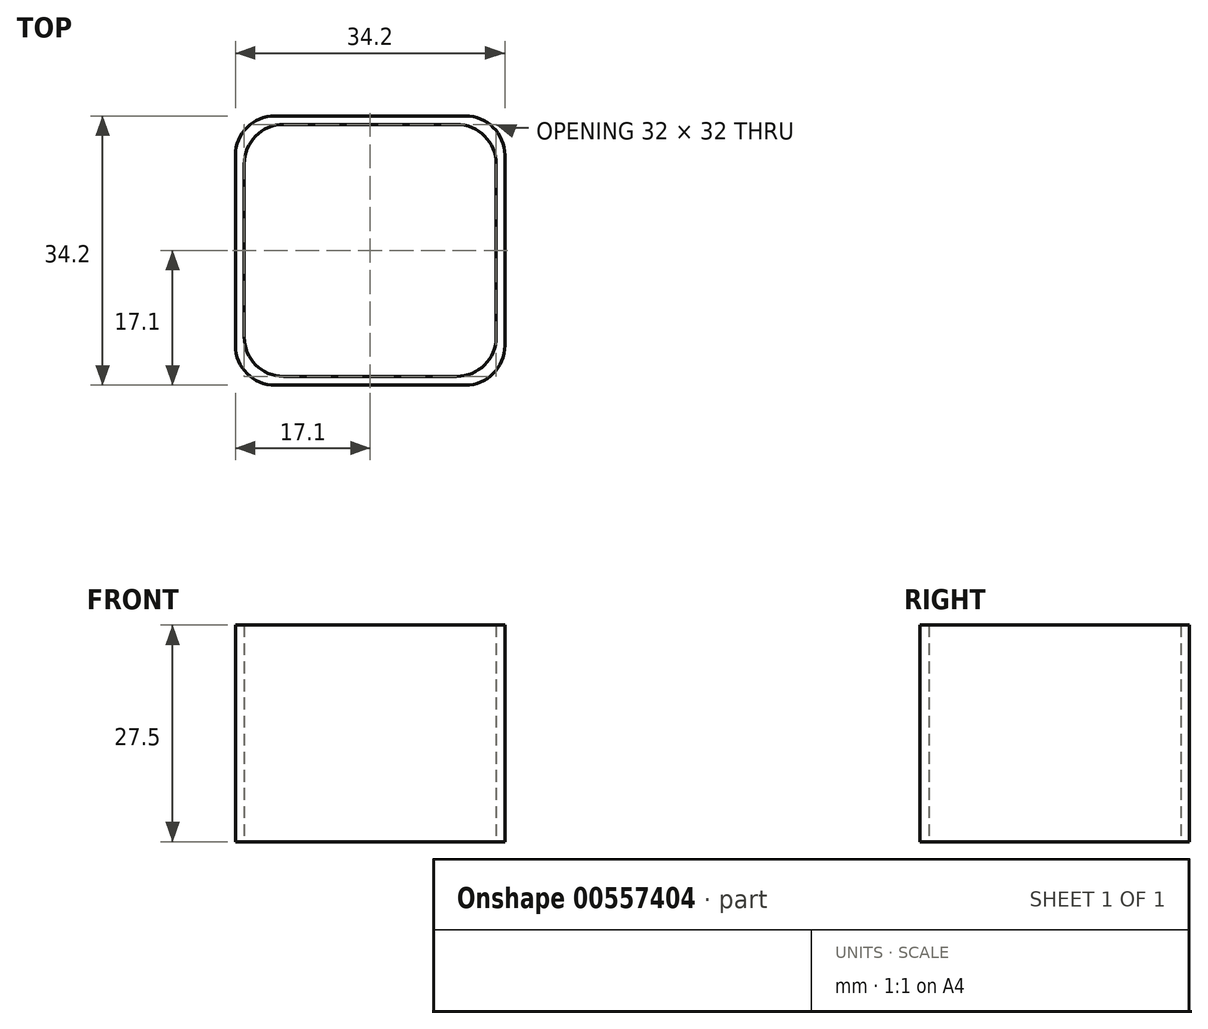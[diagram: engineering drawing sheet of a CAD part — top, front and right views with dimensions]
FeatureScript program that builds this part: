
annotation { "Feature Type Name" : "Feature", "Feature Type Description" : "" }
export const myFeature = defineFeature(function(context is Context, id is Id, definition is map)
    precondition{}
    {
        {
            var Q0;
            Q0=qCreatedBy(makeId("Top.planeOp"),FACE);
            var sketch = newSketch(context, id + "F0", { "sketchPlane" : qUnion([Q0])});
            skLineSegment(sketch, "E0.bottom", {"start": v(-17, 17) * mm, "end": v(15, 17) * mm});
            skLineSegment(sketch, "E0.top", {"start": v(-17, -15) * mm, "end": v(15, -15) * mm});
            skLineSegment(sketch, "E0.left", {"start": v(-17, 17) * mm, "end": v(-17, -15) * mm});
            skLineSegment(sketch, "E0.right", {"start": v(15, 17) * mm, "end": v(15, -15) * mm});
            skLineSegment(sketch, "E1.0", {"start": v(-15, 15) * mm, "end": v(13, 15) * mm, "construction": true});
            skLineSegment(sketch, "E1.1", {"start": v(-15, 15) * mm, "end": v(-15, -13) * mm, "construction": true});
            skLineSegment(sketch, "E1.2", {"start": v(-15, -13) * mm, "end": v(13, -13) * mm, "construction": true});
            skLineSegment(sketch, "E1.3", {"start": v(13, 15) * mm, "end": v(13, -13) * mm, "construction": true});
            skLineSegment(sketch, "E2.0", {"start": v(16.1, 18.1) * mm, "end": v(16.1, -16.1) * mm});
            skLineSegment(sketch, "E2.1", {"start": v(-18.1, 18.1) * mm, "end": v(16.1, 18.1) * mm});
            skLineSegment(sketch, "E2.2", {"start": v(-18.1, 18.1) * mm, "end": v(-18.1, -16.1) * mm});
            skLineSegment(sketch, "E2.3", {"start": v(-18.1, -16.1) * mm, "end": v(16.1, -16.1) * mm});
            skSolve(sketch);
        }
        {
            var Q0;
            Q0=makeQuery(id+"F0.imprint","IMPRINT",FACE,{"disambiguationData":[TD([[makeQuery(id+"F0.imprint","IMPRINT",EDGE,{"derivedFrom":sQuery(id+"F0.wireOp",EDGE,"E0.bottom")}),1.0]])]});
            extrude(context, id + "F1", {"entities" : qUnion([Q0]), "depth" : 27.5 * mm, "offsetDistance" : 25 * mm});
        }
        {
            var Q0;
            Q0=makeQuery(id+"F1.opExtrude","SWEPT_EDGE",EDGE,{"disambiguationData":[OSD([sQuery(id+"F0.wireOp",EDGE,"E2.0"),sQuery(id+"F0.wireOp",EDGE,"E2.3")])]});
            var Q1;
            Q1=makeQuery(id+"F1.opExtrude","SWEPT_EDGE",EDGE,{"disambiguationData":[OSD([sQuery(id+"F0.wireOp",EDGE,"E2.0"),sQuery(id+"F0.wireOp",EDGE,"E2.1")])]});
            var Q2;
            Q2=makeQuery(id+"F1.opExtrude","SWEPT_EDGE",EDGE,{"disambiguationData":[OSD([sQuery(id+"F0.wireOp",EDGE,"E2.2"),sQuery(id+"F0.wireOp",EDGE,"E2.3")])]});
            var Q3;
            Q3=makeQuery(id+"F1.opExtrude","SWEPT_EDGE",EDGE,{"disambiguationData":[OSD([sQuery(id+"F0.wireOp",EDGE,"E0.bottom"),sQuery(id+"F0.wireOp",EDGE,"E0.left")])]});
            var Q4;
            Q4=makeQuery(id+"F1.opExtrude","SWEPT_EDGE",EDGE,{"disambiguationData":[OSD([sQuery(id+"F0.wireOp",EDGE,"E0.top"),sQuery(id+"F0.wireOp",EDGE,"E0.left")])]});
            var Q5;
            Q5=makeQuery(id+"F1.opExtrude","SWEPT_EDGE",EDGE,{"disambiguationData":[OSD([sQuery(id+"F0.wireOp",EDGE,"E0.top"),sQuery(id+"F0.wireOp",EDGE,"E0.right")])]});
            var Q6;
            Q6=makeQuery(id+"F1.opExtrude","SWEPT_EDGE",EDGE,{"disambiguationData":[OSD([sQuery(id+"F0.wireOp",EDGE,"E0.bottom"),sQuery(id+"F0.wireOp",EDGE,"E0.right")])]});
            var Q7;
            Q7=makeQuery(id+"F1.opExtrude","SWEPT_EDGE",EDGE,{"disambiguationData":[OSD([sQuery(id+"F0.wireOp",EDGE,"E2.1"),sQuery(id+"F0.wireOp",EDGE,"E2.2")])]});
            fillet(context, id + "F2", {"entities" : qUnion([Q0, Q1, Q2, Q3, Q4, Q5, Q6, Q7]), "radius" : 5 * mm, "tangentPropagation" : true, "allowEdgeOverflow" : false});
        }
    });
